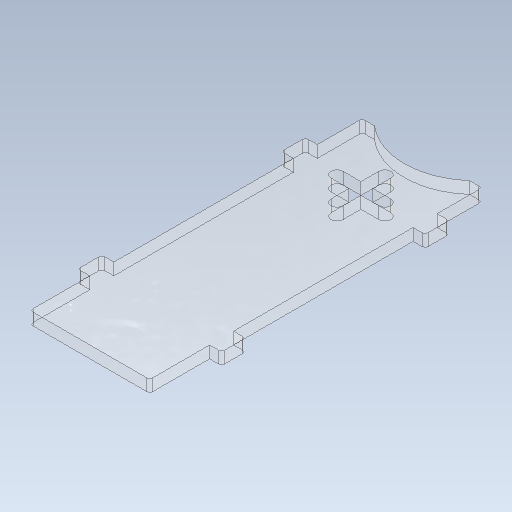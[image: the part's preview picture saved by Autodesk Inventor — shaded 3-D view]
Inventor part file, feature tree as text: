
AUTODESK INVENTOR PART (.ipt)
format: ipt  version: 2021 (Build 250183000, 183)  size: 177,664 bytes
history: native  units: mm
features: extrude x2, sketch x2
ambient origin geometry x8: Origin, YZ Plane, XZ Plane, XY Plane, X Axis, Y Axis, Z Axis, Center Point
bodies: Solid1 (feature_tree)
feature tree (4):
  extrude  "Extrusion1"  Depth=2.0mm
  sketch  "Sketch2"  dims[d4=4.0mm d5=15.0mm d6=4.0mm d7=15.0mm d8=2.0mm d9=4.0mm d10=15.0mm d11=4.0mm d12=0.5mm d13=9.0mm d14=12.0mm d15=0.5mm d16=2.0mm d17=0.0mm d18=4.0mm d19=2.0mm d20=4.0mm d21=2.0mm d22=2.0mm d23=0.0mm d26=0.0mm d27=0.5mm d28=0.0mm d29=5.0mm]
  extrude  "Extrusion2"  Depth=0.5mm
  sketch  "Sketch1"  dims[d2=15.0mm d3=2.0mm]
